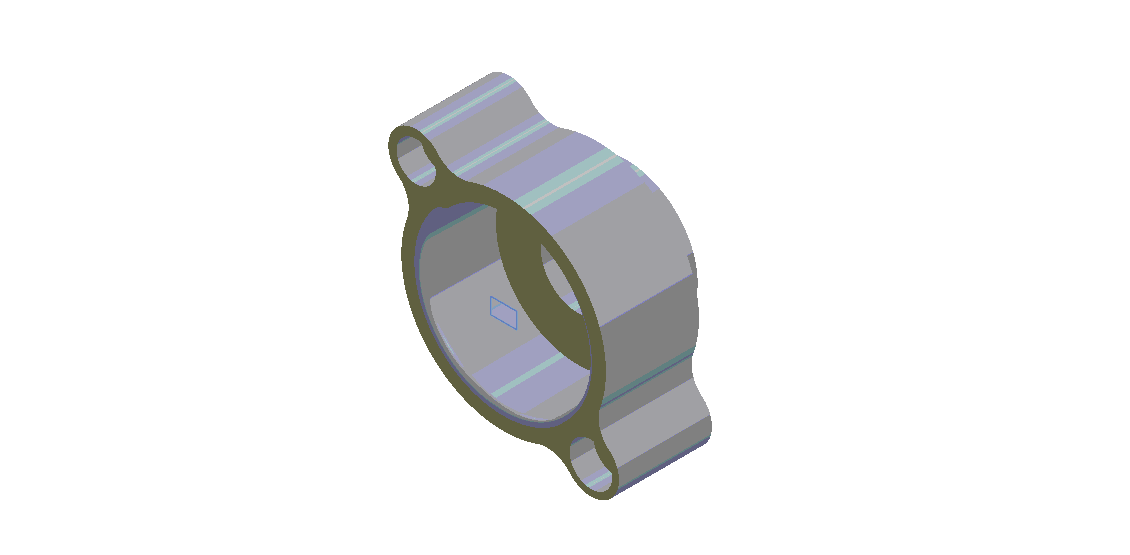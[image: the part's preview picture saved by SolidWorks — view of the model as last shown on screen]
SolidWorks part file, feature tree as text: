
SOLIDWORKS PART (.sldprt)
format: sldprt  version: not decoded by parser v0  size: 208,896 bytes
history: native  units: mm
features: sketch x8, plane x4, extrude x2, cut_extrude x2, hole x2, material x1, fillet x1 (+10 scaffold rows collapsed)
feature tree (30):
  scaffold x10  (default folders/planes/origin — collapsed)
  material  "Matériau <non spécifié>"
  plane  "FRONT"
  plane  "TOP"
  plane  "RIGHT"
  plane  "Plan1"  Offset=838.2mm
  sketch  "Esquisse1"
  extrude  "Boss.-Extru.1"  Depth=635mm
  sketch  "Esquisse2"
  extrude  "Boss.-Extru.2"  Depth=203.2mm
  sketch  "Esquisse3"
  cut_extrude  "Enlèv. mat.-Extru.1"  Depth=508mm
  sketch  "Esquisse4"
  cut_extrude  "Enlèv. mat.-Extru.2"  Depth=330.2mm
  hole  "Perçage1"  Diameter=139.7mm Depth=838.2mm
  sketch  "Esquisse6"
  sketch  "Esquisse5"  dims[Diamètre=139.7mm Profondeur=838.2mm Diamètre chambrage=266.7mm Profondeur chambrage=165.1mm]
  hole  "Perçage2"  Diameter=139.7mm Depth=838.2mm
  sketch  "Esquisse8"
  sketch  "Esquisse7"  dims[Diamètre=139.7mm Profondeur=838.2mm Diamètre chambrage=292.1mm Profondeur chambrage=165.1mm]
  fillet  "Congé1"  Radius=38.1mm
decode coverage: 9 of 15 modeling features carry decoded parameters
note: suppression state not decoded; provenance and decode notes live in map.json
